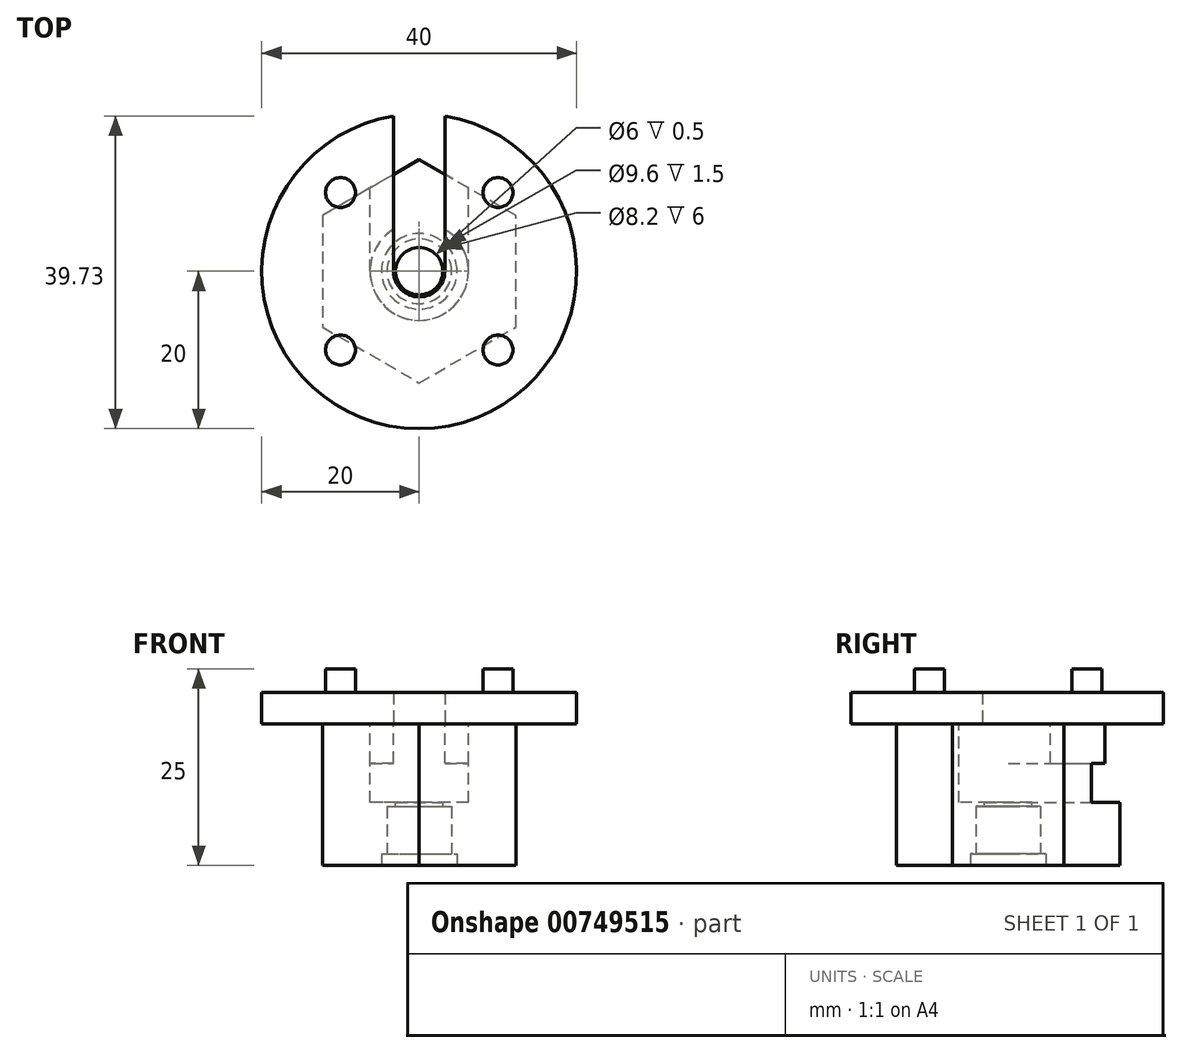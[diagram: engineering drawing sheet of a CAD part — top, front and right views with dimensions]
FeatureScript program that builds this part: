
annotation { "Feature Type Name" : "Feature", "Feature Type Description" : "" }
export const myFeature = defineFeature(function(context is Context, id is Id, definition is map)
    precondition{}
    {
        {
            var Q0;
            Q0=qCreatedBy(makeId("Top.planeOp"),FACE);
            var sketch = newSketch(context, id + "F0", { "sketchPlane" : qUnion([Q0])});
            skCircle(sketch, "E0", {"center": v(0, 0) * mm, "radius": 20 * mm});
            skLineSegment(sketch, "E1.bottom", {"start": v(10, -10) * mm, "end": v(-10, -10) * mm, "construction": true});
            skLineSegment(sketch, "E1.top", {"start": v(10, 10) * mm, "end": v(-10, 10) * mm, "construction": true});
            skLineSegment(sketch, "E1.left", {"start": v(10, -10) * mm, "end": v(10, 10) * mm, "construction": true});
            skLineSegment(sketch, "E1.right", {"start": v(-10, -10) * mm, "end": v(-10, 10) * mm, "construction": true});
            skCircle(sketch, "E2", {"center": v(-10, 10) * mm, "radius": 1.9 * mm});
            skCircle(sketch, "E3", {"center": v(10, 10) * mm, "radius": 1.9 * mm});
            skCircle(sketch, "E4", {"center": v(10, -10) * mm, "radius": 1.9 * mm});
            skCircle(sketch, "E5", {"center": v(-10, -10) * mm, "radius": 1.9 * mm});
            skCircle(sketch, "E6", {"center": v(0, 0) * mm, "radius": 3.25 * mm});
            skLineSegment(sketch, "E7", {"start": v(-3.25, 0) * mm, "end": v(-3.25, 19.73) * mm});
            skLineSegment(sketch, "E8", {"start": v(3.25, 0) * mm, "end": v(3.25, 19.73) * mm});
            skSolve(sketch);
        }
        {
            var Q0;
            Q0=makeQuery(id+"F0.imprint","IMPRINT",FACE,{"disambiguationData":[TD([[makeQuery(id+"F0.imprint","IMPRINT",EDGE,{"derivedFrom":sQuery(id+"F0.wireOp",EDGE,"E2")}),1.0]])]});
            var Q1;
            Q1=makeQuery(id+"F0.imprint","IMPRINT",FACE,{"disambiguationData":[TD([[makeQuery(id+"F0.imprint","IMPRINT",EDGE,{"derivedFrom":sQuery(id+"F0.wireOp",EDGE,"E3")}),1.0]])]});
            var Q2;
            Q2=makeQuery(id+"F0.imprint","IMPRINT",FACE,{"disambiguationData":[TD([[makeQuery(id+"F0.imprint","IMPRINT",EDGE,{"derivedFrom":sQuery(id+"F0.wireOp",EDGE,"E4")}),1.0]])]});
            var Q3;
            Q3=makeQuery(id+"F0.imprint","IMPRINT",FACE,{"disambiguationData":[TD([[makeQuery(id+"F0.imprint","IMPRINT",EDGE,{"derivedFrom":sQuery(id+"F0.wireOp",EDGE,"E5")}),1.0]])]});
            var Q4;
            Q4=makeQuery(id+"F0.imprint","IMPRINT",FACE,{"disambiguationData":[TD([[makeQuery(id+"F0.imprint","IMPRINT",EDGE,{"derivedFrom":sQuery(id+"F0.wireOp",EDGE,"E2")}),-1.0]])]});
            extrude(context, id + "F1", {"entities" : qUnion([Q0, Q1, Q2, Q3, Q4]), "depth" : 4 * mm, "offsetDistance" : 25 * mm});
        }
        {
            var Q0;
            Q0=makeQuery(id+"F0.imprint","IMPRINT",FACE,{"disambiguationData":[TD([[makeQuery(id+"F0.imprint","IMPRINT",EDGE,{"derivedFrom":sQuery(id+"F0.wireOp",EDGE,"E2")}),1.0]])]});
            var Q1;
            Q1=makeQuery(id+"F0.imprint","IMPRINT",FACE,{"disambiguationData":[TD([[makeQuery(id+"F0.imprint","IMPRINT",EDGE,{"derivedFrom":sQuery(id+"F0.wireOp",EDGE,"E3")}),1.0]])]});
            var Q2;
            Q2=makeQuery(id+"F0.imprint","IMPRINT",FACE,{"disambiguationData":[TD([[makeQuery(id+"F0.imprint","IMPRINT",EDGE,{"derivedFrom":sQuery(id+"F0.wireOp",EDGE,"E4")}),1.0]])]});
            var Q3;
            Q3=makeQuery(id+"F0.imprint","IMPRINT",FACE,{"disambiguationData":[TD([[makeQuery(id+"F0.imprint","IMPRINT",EDGE,{"derivedFrom":sQuery(id+"F0.wireOp",EDGE,"E5")}),1.0]])]});
            extrude(context, id + "F2", {"entities" : qUnion([Q0, Q1, Q2, Q3]), "operationType" : NewBodyOperationType.ADD, "depth" : 7 * mm, "offsetDistance" : 25 * mm});
        }
        {
            var Q0;
            Q0=makeQuery(id+"F1.opExtrude","CAP_FACE",FACE,{"disambiguationData":[OSD([sQuery(id+"F0.wireOp",EDGE,"E0"),sQuery(id+"F0.wireOp",EDGE,"E6"),sQuery(id+"F0.wireOp",EDGE,"E7"),sQuery(id+"F0.wireOp",EDGE,"E8")])],"isStart":true});
            var sketch = newSketch(context, id + "F3", { "sketchPlane" : qUnion([Q0])});
            skCircle(sketch, "E9", {"center": v(0, 0) * mm, "radius": 6.25 * mm});
            skCircle(sketch, "E10.cCircle", {"center": v(0, 0) * mm, "radius": 14.18 * mm, "construction": true});
            skLineSegment(sketch, "E10.0", {"start": v(0, 14.18) * mm, "end": v(12.28, 7.09) * mm});
            skLineSegment(sketch, "E10.1", {"start": v(12.28, 7.09) * mm, "end": v(12.28, -7.09) * mm});
            skLineSegment(sketch, "E10.2", {"start": v(12.28, -7.09) * mm, "end": v(0, -14.18) * mm});
            skLineSegment(sketch, "E10.3", {"start": v(0, -14.18) * mm, "end": v(-12.28, -7.09) * mm});
            skLineSegment(sketch, "E10.4", {"start": v(-12.28, -7.09) * mm, "end": v(-12.28, 7.09) * mm});
            skLineSegment(sketch, "E10.5", {"start": v(-12.28, 7.09) * mm, "end": v(0, 14.18) * mm});
            skSolve(sketch);
        }
        {
            var Q0;
            Q0=makeQuery(id+"F3.imprint","IMPRINT",FACE,{"disambiguationData":[TD([[makeQuery(id+"F3.imprint","IMPRINT",EDGE,{"derivedFrom":sQuery(id+"F3.wireOp",EDGE,"E10.0")}),-1.0]])]});
            extrude(context, id + "F4", {"entities" : qUnion([Q0]), "operationType" : NewBodyOperationType.ADD, "depth" : 5 * mm, "offsetDistance" : 25 * mm});
        }
        {
            var Q0;
            Q0=makeQuery(id+"F4.opExtrude","CAP_FACE",FACE,{"disambiguationData":[OSD([sQuery(id+"F0.wireOp",EDGE,"E7"),sQuery(id+"F0.wireOp",EDGE,"E8"),sQuery(id+"F3.wireOp",EDGE,"E9"),sQuery(id+"F3.wireOp",EDGE,"E10.0"),sQuery(id+"F3.wireOp",EDGE,"E10.1"),sQuery(id+"F3.wireOp",EDGE,"E10.2"),sQuery(id+"F3.wireOp",EDGE,"E10.3"),sQuery(id+"F3.wireOp",EDGE,"E10.4"),sQuery(id+"F3.wireOp",EDGE,"E10.5")])],"isStart":false});
            var sketch = newSketch(context, id + "F5", { "sketchPlane" : qUnion([Q0])});
            skCircle(sketch, "E11", {"center": v(0, 0) * mm, "radius": 6.25 * mm});
            skLineSegment(sketch, "E12", {"start": v(-6.25, 0) * mm, "end": v(-6.25, -10.57) * mm});
            skLineSegment(sketch, "E13", {"start": v(6.25, 0) * mm, "end": v(6.25, -10.57) * mm});
            skSolve(sketch);
        }
        {
            var Q0;
            {var subQ0=sQuery(id+"F5.wireOp",EDGE,"E12");Q0=makeQuery(id+"F5.imprint","IMPRINT",FACE,{"disambiguationData":[TD([[makeQuery(id+"F5.imprint","IMPRINT",EDGE,{"derivedFrom":subQ0}),-1.0]])]});}
            extrude(context, id + "F6", {"entities" : qUnion([Q0]), "operationType" : NewBodyOperationType.ADD, "depth" : 5 * mm, "offsetDistance" : 25 * mm});
        }
        {
            var Q0;
            Q0=makeQuery(id+"F6.opExtrude","CAP_FACE",FACE,{"disambiguationData":[OSD([sQuery(id+"F3.wireOp",EDGE,"E10.0"),sQuery(id+"F3.wireOp",EDGE,"E10.1"),sQuery(id+"F3.wireOp",EDGE,"E10.2"),sQuery(id+"F3.wireOp",EDGE,"E10.3"),sQuery(id+"F3.wireOp",EDGE,"E10.4"),sQuery(id+"F3.wireOp",EDGE,"E10.5"),sQuery(id+"F5.wireOp",EDGE,"E11"),sQuery(id+"F5.wireOp",EDGE,"E12"),sQuery(id+"F5.wireOp",EDGE,"E13")])],"isStart":false});
            var sketch = newSketch(context, id + "F7", { "sketchPlane" : qUnion([Q0])});
            skCircle(sketch, "E14", {"center": v(0, 0) * mm, "radius": 6.25 * mm});
            skCircle(sketch, "E15.cCircle", {"center": v(0, 0) * mm, "radius": 14.18 * mm, "construction": true});
            skLineSegment(sketch, "E15.0", {"start": v(0, 14.18) * mm, "end": v(12.28, 7.09) * mm});
            skLineSegment(sketch, "E15.1", {"start": v(12.28, 7.09) * mm, "end": v(12.28, -7.09) * mm});
            skLineSegment(sketch, "E15.2", {"start": v(12.28, -7.09) * mm, "end": v(0, -14.18) * mm});
            skLineSegment(sketch, "E15.3", {"start": v(0, -14.18) * mm, "end": v(-12.28, -7.09) * mm});
            skLineSegment(sketch, "E15.4", {"start": v(-12.28, -7.09) * mm, "end": v(-12.28, 7.09) * mm});
            skLineSegment(sketch, "E15.5", {"start": v(-12.28, 7.09) * mm, "end": v(0, 14.18) * mm});
            skCircle(sketch, "E16", {"center": v(0, 0) * mm, "radius": 3 * mm});
            skSolve(sketch);
        }
        {
            var Q0;
            Q0=makeQuery(id+"F7.imprint","IMPRINT",FACE,{"disambiguationData":[TD([[makeQuery(id+"F7.imprint","IMPRINT",EDGE,{"derivedFrom":sQuery(id+"F7.wireOp",EDGE,"E15.0")}),-1.0]])]});
            var Q1;
            Q1=makeQuery(id+"F7.imprint","IMPRINT",FACE,{"disambiguationData":[TD([[makeQuery(id+"F7.imprint","IMPRINT",EDGE,{"derivedFrom":sQuery(id+"F7.wireOp",EDGE,"E16")}),-1.0]])]});
            var Q2;
            {var subQ4=makeQuery(id+"F6.opExtrude","CAP_EDGE",EDGE,{"disambiguationData":[OSD([sQuery(id+"F5.wireOp",EDGE,"E12")])],"isStart":false});Q2=makeQuery(id+"F7.imprint","IMPRINT",FACE,{"disambiguationData":[TD([[makeQuery(id+"F7.imprint","IMPRINT",EDGE,{"derivedFrom":subQ4}),1.0]])]});}
            extrude(context, id + "F8", {"entities" : qUnion([Q0, Q1, Q2]), "operationType" : NewBodyOperationType.ADD, "depth" : 8 * mm, "offsetDistance" : 25 * mm});
        }
        {
            var Q0;
            Q0=makeQuery(id+"F8.opExtrude","CAP_FACE",FACE,{"disambiguationData":[OSD([sQuery(id+"F7.wireOp",EDGE,"E15.0"),sQuery(id+"F7.wireOp",EDGE,"E15.1"),sQuery(id+"F7.wireOp",EDGE,"E15.2"),sQuery(id+"F7.wireOp",EDGE,"E15.3"),sQuery(id+"F7.wireOp",EDGE,"E15.4"),sQuery(id+"F7.wireOp",EDGE,"E15.5"),sQuery(id+"F7.wireOp",EDGE,"E16")])],"isStart":false});
            var sketch = newSketch(context, id + "F9", { "sketchPlane" : qUnion([Q0])});
            skCircle(sketch, "E17", {"center": v(0, 0) * mm, "radius": 4.8 * mm});
            skCircle(sketch, "E18", {"center": v(0, 0) * mm, "radius": 4.1 * mm});
            skSolve(sketch);
        }
        {
            var Q0;
            Q0=makeQuery(id+"F9.imprint","IMPRINT",FACE,{"disambiguationData":[TD([[makeQuery(id+"F9.imprint","IMPRINT",EDGE,{"derivedFrom":sQuery(id+"F9.wireOp",EDGE,"E17")}),1.0]])]});
            extrude(context, id + "F10", {"entities" : qUnion([Q0]), "operationType" : NewBodyOperationType.REMOVE, "oppositeDirection" : true, "depth" : 1.5 * mm, "offsetDistance" : 25 * mm});
        }
        {
            var Q0;
            Q0=makeQuery(id+"F9.imprint","IMPRINT",FACE,{"disambiguationData":[TD([[makeQuery(id+"F9.imprint","IMPRINT",EDGE,{"derivedFrom":sQuery(id+"F9.wireOp",EDGE,"E18")}),1.0]])]});
            extrude(context, id + "F11", {"entities" : qUnion([Q0]), "operationType" : NewBodyOperationType.REMOVE, "oppositeDirection" : true, "depth" : 7.5 * mm, "offsetDistance" : 25 * mm});
        }
    });
